# Revit family: 9705_Skydedør_Højre_Coto62
name_source: partatom
category: Doors
revit_build: Autodesk Revit LT 2016 (Build: 20150220_1215(x64)
units: mm (PartAtom-declared; Revit-internal decimal feet)

## family parameters
Always vertical = Yes
Cut with Voids When Loaded = No
Host = Wall
OmniClass Number = 23.30.10.00
OmniClass Title = Doors
Room Calculation Point = No
Shared = No

## types (1)
- 3000x2100mm
    Bottom Placement = 109 mm  [stored 0.357612 ft]
    Frame Projection Ext. = 25 mm  [stored 0.082021 ft]
    Frame Projection Int. = 25 mm  [stored 0.082021 ft]
    Frame Width = 75 mm  [stored 0.246063 ft]
    Function = Interior
    Height = 2100 mm
    Joint = 12 mm  [stored 0.0393701 ft]
    Manufacturer = www.kronevinduer.dk
    Placement in wall = 50 mm  [stored 0.164042 ft]
    Rough Height = 2124 mm  [stored 6.9685 ft]
    Rough Width = 3024 mm  [stored 9.92126 ft]
    Sash placement in wall = 226 mm  [stored 0.74147 ft]
    Wall Closure = By host
    Width = 3000 mm  [stored 9.84252 ft]

note: [stored X ft] marks values corroborated as IEEE doubles in the binary element streams (Revit-internal decimal feet)

## geometry (parser evidence)
native form markers: Sweep x10
no freeform markers — native parametric forms only
